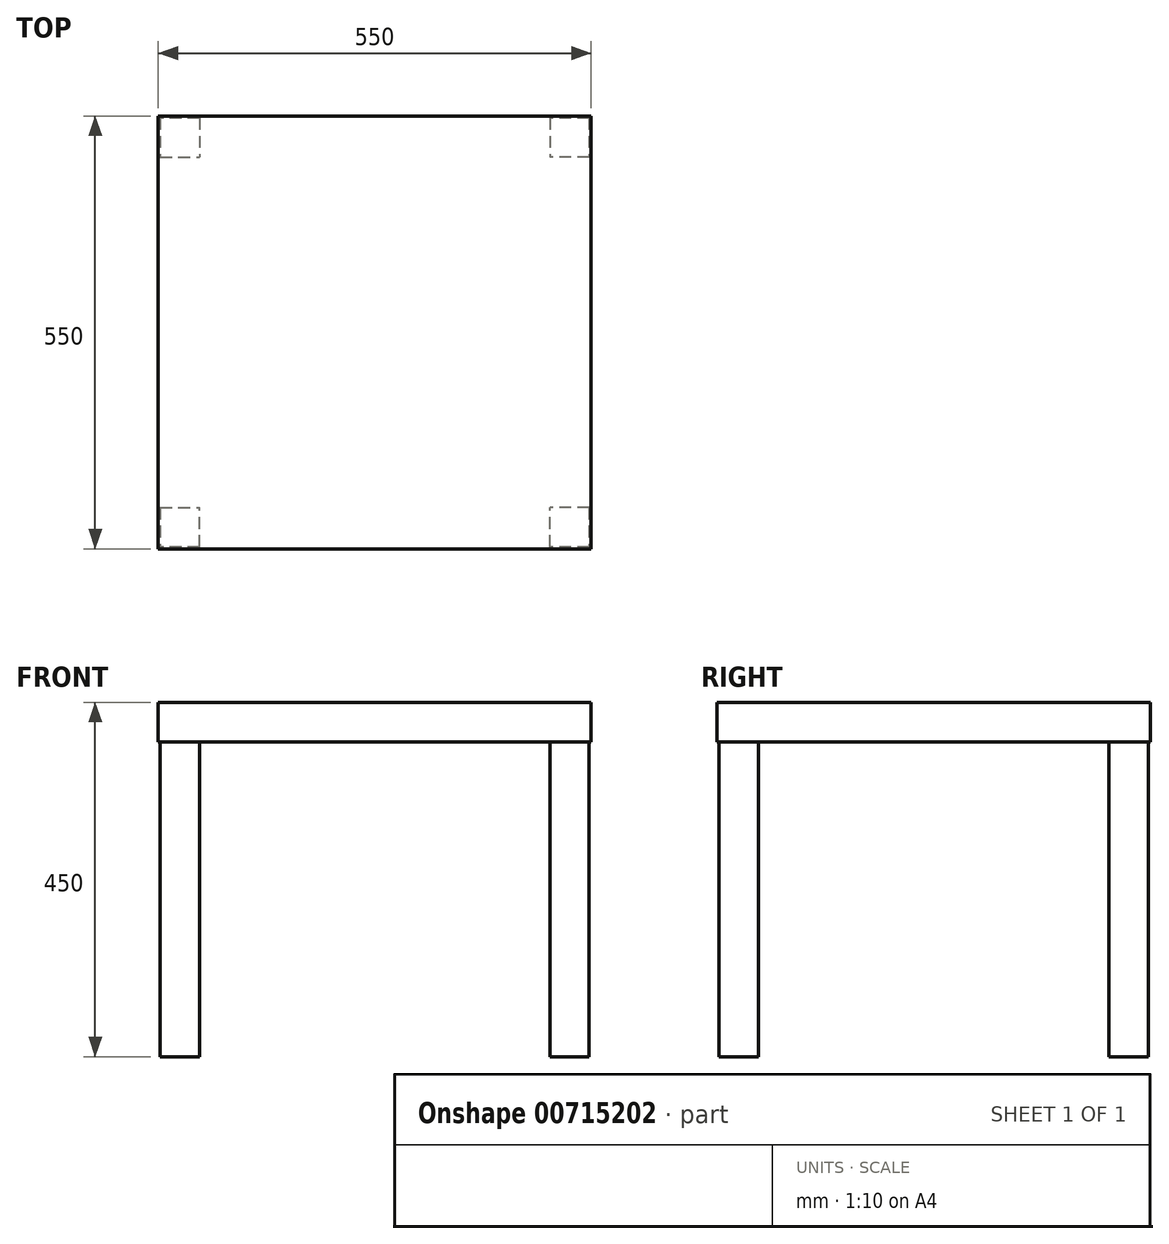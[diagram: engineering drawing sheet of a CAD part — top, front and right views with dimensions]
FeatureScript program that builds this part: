
annotation { "Feature Type Name" : "Feature", "Feature Type Description" : "" }
export const myFeature = defineFeature(function(context is Context, id is Id, definition is map)
    precondition{}
    {
        {
            var Q0;
            Q0=qCreatedBy(makeId("Top.planeOp"),FACE);
            var sketch = newSketch(context, id + "F0", { "sketchPlane" : qUnion([Q0])});
            skLineSegment(sketch, "E0.bottom", {"start": v(275, 275) * mm, "end": v(-275, 275) * mm});
            skLineSegment(sketch, "E0.top", {"start": v(275, -275) * mm, "end": v(-275, -275) * mm});
            skLineSegment(sketch, "E0.left", {"start": v(275, 275) * mm, "end": v(275, -275) * mm});
            skLineSegment(sketch, "E0.right", {"start": v(-275, 275) * mm, "end": v(-275, -275) * mm});
            skPoint(sketch, "E0.middle", {"position": v(0, 0) * mm});
            skLineSegment(sketch, "E1.0", {"start": v(272.5, 272.5) * mm, "end": v(-272.5, 272.5) * mm});
            skLineSegment(sketch, "E1.1", {"start": v(272.5, 272.5) * mm, "end": v(272.5, -272.5) * mm});
            skLineSegment(sketch, "E1.2", {"start": v(272.5, -272.5) * mm, "end": v(-272.5, -272.5) * mm});
            skLineSegment(sketch, "E1.3", {"start": v(-272.5, 272.5) * mm, "end": v(-272.5, -272.5) * mm});
            skLineSegment(sketch, "E2.bottom", {"start": v(-272.5, 272.5) * mm, "end": v(-222.5, 272.5) * mm});
            skLineSegment(sketch, "E2.top", {"start": v(-272.5, 222.5) * mm, "end": v(-222.5, 222.5) * mm});
            skLineSegment(sketch, "E2.left", {"start": v(-272.5, 272.5) * mm, "end": v(-272.5, 222.5) * mm});
            skLineSegment(sketch, "E2.right", {"start": v(-222.5, 272.5) * mm, "end": v(-222.5, 222.5) * mm});
            skLineSegment(sketch, "E3", {"start": v(0, 275) * mm, "end": v(0, -272.5) * mm, "construction": true});
            skLineSegment(sketch, "E4", {"start": v(-272.5, 0) * mm, "end": v(272.5, 0) * mm, "construction": true});
            skLineSegment(sketch, "E5.MirrorCS", {"start": v(272.5, 222.5) * mm, "end": v(222.5, 222.5) * mm});
            skLineSegment(sketch, "E6.MirrorCS", {"start": v(222.5, 272.5) * mm, "end": v(222.5, 222.5) * mm});
            skLineSegment(sketch, "E7.MirrorCS", {"start": v(-272.5, -222.5) * mm, "end": v(-222.5, -222.5) * mm});
            skLineSegment(sketch, "E8.MirrorCS", {"start": v(-222.5, -272.5) * mm, "end": v(-222.5, -222.5) * mm});
            skLineSegment(sketch, "E9.MirrorCS", {"start": v(222.5, -272.5) * mm, "end": v(222.5, -222.5) * mm});
            skLineSegment(sketch, "E10.MirrorCS", {"start": v(272.5, -222.5) * mm, "end": v(222.5, -222.5) * mm});
            skSolve(sketch);
        }
        {
            var Q0;
            {var subQ3=sQuery(id+"F0.wireOp",EDGE,"E2.top");Q0=makeQuery(id+"F0.imprint","IMPRINT",FACE,{"disambiguationData":[TD([[makeQuery(id+"F0.imprint","IMPRINT",EDGE,{"derivedFrom":subQ3}),-1.0]])]});}
            var Q1;
            Q1=makeQuery(id+"F0.imprint","IMPRINT",FACE,{"disambiguationData":[TD([[makeQuery(id+"F0.imprint","IMPRINT",EDGE,{"derivedFrom":sQuery(id+"F0.wireOp",EDGE,"E0.bottom")}),1.0]])]});
            extrude(context, id + "F1", {"entities" : qUnion([Q0, Q1]), "depth" : 50 * mm, "offsetDistance" : 25 * mm});
        }
        {
            var Q0;
            {var subQ4=sQuery(id+"F0.wireOp",EDGE,"E7.MirrorCS");Q0=makeQuery(id+"F0.imprint","IMPRINT",FACE,{"disambiguationData":[TD([[makeQuery(id+"F0.imprint","IMPRINT",EDGE,{"derivedFrom":subQ4}),-1.0]])]});}
            var Q1;
            {var subQ4=sQuery(id+"F0.wireOp",EDGE,"E9.MirrorCS");Q1=makeQuery(id+"F0.imprint","IMPRINT",FACE,{"disambiguationData":[TD([[makeQuery(id+"F0.imprint","IMPRINT",EDGE,{"derivedFrom":subQ4}),-1.0]])]});}
            var Q2;
            {var subQ4=sQuery(id+"F0.wireOp",EDGE,"E5.MirrorCS");Q2=makeQuery(id+"F0.imprint","IMPRINT",FACE,{"disambiguationData":[TD([[makeQuery(id+"F0.imprint","IMPRINT",EDGE,{"derivedFrom":subQ4}),-1.0]])]});}
            var Q3;
            {var subQ4=sQuery(id+"F0.wireOp",EDGE,"E2.top");Q3=makeQuery(id+"F0.imprint","IMPRINT",FACE,{"disambiguationData":[TD([[makeQuery(id+"F0.imprint","IMPRINT",EDGE,{"derivedFrom":subQ4}),1.0]])]});}
            extrude(context, id + "F2", {"entities" : qUnion([Q0, Q1, Q2, Q3]), "operationType" : NewBodyOperationType.ADD, "depth" : 50 * mm, "offsetDistance" : 25 * mm, "hasSecondDirection" : true, "secondDirectionOppositeDirection" : true, "secondDirectionDepth" : 400 * mm});
        }
    });
